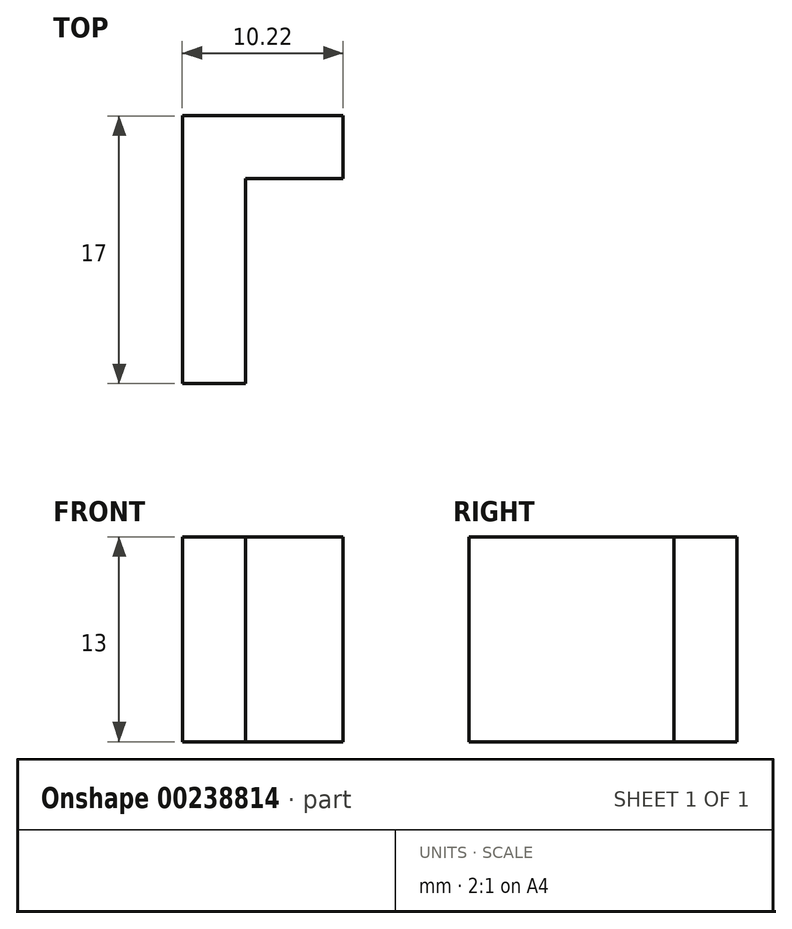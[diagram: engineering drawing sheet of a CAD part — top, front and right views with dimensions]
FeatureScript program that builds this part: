
annotation { "Feature Type Name" : "Feature", "Feature Type Description" : "" }
export const myFeature = defineFeature(function(context is Context, id is Id, definition is map)
    precondition{}
    {
        {
            var Q0;
            Q0=qCreatedBy(makeId("Top.planeOp"),FACE);
            var sketch = newSketch(context, id + "F0", { "sketchPlane" : qUnion([Q0])});
            skLineSegment(sketch, "E0.bottom", {"start": v(-64.52, 57.22) * mm, "end": v(-60.52, 57.22) * mm});
            skLineSegment(sketch, "E0.top", {"start": v(-64.52, 40.22) * mm, "end": v(-60.52, 40.22) * mm});
            skLineSegment(sketch, "E0.left", {"start": v(-64.52, 57.22) * mm, "end": v(-64.52, 40.22) * mm});
            skLineSegment(sketch, "E0.right", {"start": v(-60.52, 57.22) * mm, "end": v(-60.52, 40.22) * mm});
            skLineSegment(sketch, "E1.bottom", {"start": v(-60.52, 57.22) * mm, "end": v(-54.3, 57.22) * mm});
            skLineSegment(sketch, "E1.top", {"start": v(-60.52, 53.24) * mm, "end": v(-54.3, 53.24) * mm});
            skLineSegment(sketch, "E1.left", {"start": v(-60.52, 57.22) * mm, "end": v(-60.52, 53.24) * mm});
            skLineSegment(sketch, "E1.right", {"start": v(-54.3, 57.22) * mm, "end": v(-54.3, 53.24) * mm});
            skSolve(sketch);
        }
        {
            var Q0;
            Q0=makeQuery(id+"F0.imprint","IMPRINT",FACE,{"disambiguationData":[TD([[makeQuery(id+"F0.imprint","IMPRINT",EDGE,{"derivedFrom":sQuery(id+"F0.wireOp",EDGE,"E0.bottom")}),-1.0]])]});
            var Q1;
            Q1=makeQuery(id+"F0.imprint","IMPRINT",FACE,{"disambiguationData":[TD([[makeQuery(id+"F0.imprint","IMPRINT",EDGE,{"derivedFrom":sQuery(id+"F0.wireOp",EDGE,"E1.bottom")}),-1.0]])]});
            var Q2;
            Q2 = qSketchRegion(id + "F0", true);
            extrude(context, id + "F1", {"entities" : qUnion([Q0, Q1, Q2]), "depth" : 13 * mm});
        }
    });
